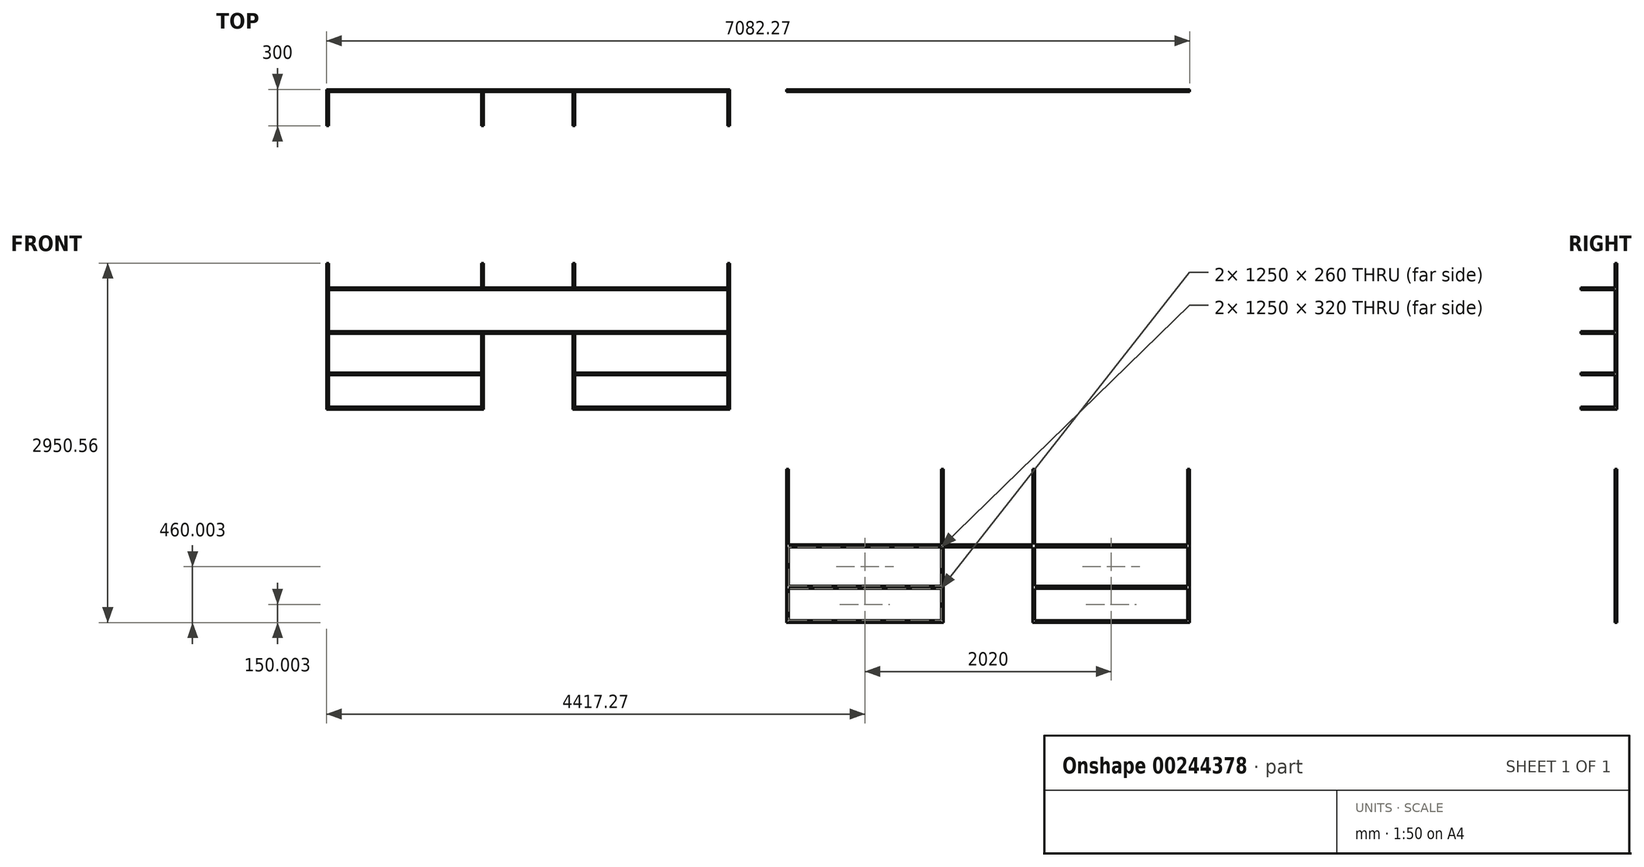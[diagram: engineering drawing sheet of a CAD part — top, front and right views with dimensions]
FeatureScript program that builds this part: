
annotation { "Feature Type Name" : "Feature", "Feature Type Description" : "" }
export const myFeature = defineFeature(function(context is Context, id is Id, definition is map)
    precondition{}
    {
        {
            var Q0;
            Q0=qCreatedBy(makeId("Front.planeOp"),FACE);
            var sketch = newSketch(context, id + "F0", { "sketchPlane" : qUnion([Q0])});
            skLineSegment(sketch, "E0.bottom", {"start": v(0, 0) * mm, "end": v(1290, 0) * mm});
            skLineSegment(sketch, "E0.top", {"start": v(0, 1000) * mm, "end": v(1290, 1000) * mm});
            skLineSegment(sketch, "E0.left", {"start": v(0, 0) * mm, "end": v(0, 1000) * mm});
            skLineSegment(sketch, "E0.right", {"start": v(1290, 0) * mm, "end": v(1290, 1000) * mm});
            skLineSegment(sketch, "E1.bottom", {"start": v(1290, 1000) * mm, "end": v(2020, 1000) * mm});
            skLineSegment(sketch, "E1.top", {"start": v(1290, 620) * mm, "end": v(2020, 620) * mm});
            skLineSegment(sketch, "E1.left", {"start": v(1290, 1000) * mm, "end": v(1290, 620) * mm});
            skLineSegment(sketch, "E1.right", {"start": v(2020, 1000) * mm, "end": v(2020, 620) * mm});
            skLineSegment(sketch, "E2.bottom", {"start": v(2020, 1000) * mm, "end": v(3310, 1000) * mm});
            skLineSegment(sketch, "E2.top", {"start": v(2020, 0) * mm, "end": v(3310, 0) * mm});
            skLineSegment(sketch, "E2.left", {"start": v(2020, 1000) * mm, "end": v(2020, 0) * mm});
            skLineSegment(sketch, "E2.right", {"start": v(3310, 1000) * mm, "end": v(3310, 0) * mm});
            skLineSegment(sketch, "E3", {"start": v(0, 300) * mm, "end": v(1290, 300) * mm});
            skLineSegment(sketch, "E4", {"start": v(0, 620) * mm, "end": v(1290, 620) * mm});
            skLineSegment(sketch, "E5", {"start": v(2020, 620) * mm, "end": v(3310, 620) * mm});
            skLineSegment(sketch, "E6", {"start": v(2020, 300) * mm, "end": v(3310, 300) * mm});
            skLineSegment(sketch, "E7", {"start": v(20, 1000) * mm, "end": v(20, 0) * mm});
            skLineSegment(sketch, "E8", {"start": v(1270, 1000) * mm, "end": v(1270, 0) * mm});
            skLineSegment(sketch, "E9", {"start": v(0, 980) * mm, "end": v(3310, 980) * mm});
            skLineSegment(sketch, "E10", {"start": v(0, 640) * mm, "end": v(3310, 640) * mm});
            skPoint(sketch, "E11.endSnap0", {"position": v(3310, 500) * mm});
            skLineSegment(sketch, "E12", {"start": v(0, 280) * mm, "end": v(1290, 280) * mm});
            skLineSegment(sketch, "E13", {"start": v(0, 20) * mm, "end": v(1290, 20) * mm});
            skLineSegment(sketch, "E14.trimOffspring", {"start": v(2020, 280) * mm, "end": v(3310, 280) * mm});
            skLineSegment(sketch, "E15.trimOffspring", {"start": v(2020, 20) * mm, "end": v(3310, 20) * mm});
            skLineSegment(sketch, "E16", {"start": v(2040, 980) * mm, "end": v(2040, 0) * mm});
            skLineSegment(sketch, "E17", {"start": v(3290, 1000) * mm, "end": v(3290, 0) * mm});
            skLineSegment(sketch, "E18.bottom", {"start": v(3772.27, -1750.56) * mm, "end": v(5062.27, -1750.56) * mm});
            skLineSegment(sketch, "E18.left", {"start": v(3772.27, -1750.56) * mm, "end": v(3772.27, -490.56) * mm});
            skLineSegment(sketch, "E18.right", {"start": v(5062.27, -1750.56) * mm, "end": v(5062.27, -490.56) * mm});
            skLineSegment(sketch, "E19.top", {"start": v(5062.27, -1130.56) * mm, "end": v(5792.27, -1130.56) * mm});
            skLineSegment(sketch, "E19.left", {"start": v(5062.27, -490.56) * mm, "end": v(5062.27, -1130.56) * mm});
            skLineSegment(sketch, "E19.right", {"start": v(5792.27, -490.56) * mm, "end": v(5792.27, -1130.56) * mm});
            skLineSegment(sketch, "E20.top", {"start": v(5792.27, -1750.56) * mm, "end": v(7082.27, -1750.56) * mm});
            skLineSegment(sketch, "E20.left", {"start": v(5792.27, -490.56) * mm, "end": v(5792.27, -1750.56) * mm});
            skLineSegment(sketch, "E20.right", {"start": v(7082.27, -490.56) * mm, "end": v(7082.27, -1750.56) * mm});
            skLineSegment(sketch, "E21", {"start": v(3772.27, -1450.56) * mm, "end": v(5062.27, -1450.56) * mm});
            skLineSegment(sketch, "E22", {"start": v(3772.27, -1130.56) * mm, "end": v(5062.27, -1130.56) * mm});
            skLineSegment(sketch, "E23", {"start": v(5792.27, -1130.56) * mm, "end": v(7082.27, -1130.56) * mm});
            skLineSegment(sketch, "E24", {"start": v(5792.27, -1450.56) * mm, "end": v(7082.27, -1450.56) * mm});
            skLineSegment(sketch, "E25", {"start": v(3792.27, -490.56) * mm, "end": v(3792.27, -1750.56) * mm});
            skLineSegment(sketch, "E26", {"start": v(5042.27, -490.56) * mm, "end": v(5042.27, -1750.56) * mm});
            skLineSegment(sketch, "E27", {"start": v(3772.27, -1110.56) * mm, "end": v(7082.27, -1110.56) * mm});
            skPoint(sketch, "E28.endSnap0", {"position": v(7082.27, -1120.56) * mm});
            skLineSegment(sketch, "E29", {"start": v(3772.27, -1470.56) * mm, "end": v(5062.27, -1470.56) * mm});
            skLineSegment(sketch, "E30", {"start": v(3772.27, -1730.56) * mm, "end": v(5062.27, -1730.56) * mm});
            skLineSegment(sketch, "E31.trimOffspring", {"start": v(5792.27, -1470.56) * mm, "end": v(7082.27, -1470.56) * mm});
            skLineSegment(sketch, "E32.trimOffspring", {"start": v(5792.27, -1730.56) * mm, "end": v(7082.27, -1730.56) * mm});
            skLineSegment(sketch, "E33", {"start": v(5812.27, -770.56) * mm, "end": v(5812.27, -1750.56) * mm});
            skLineSegment(sketch, "E34", {"start": v(7062.27, -490.56) * mm, "end": v(7062.27, -1750.56) * mm});
            skLineSegment(sketch, "E35", {"start": v(5812.27, -770.56) * mm, "end": v(5812.27, -490.56) * mm});
            skLineSegment(sketch, "E36.trimOffspring", {"start": v(5792.27, -770.56) * mm, "end": v(5812.27, -770.56) * mm});
            skLineSegment(sketch, "E37.trimOffspring", {"start": v(7062.27, -770.56) * mm, "end": v(7082.27, -770.56) * mm});
            skLineSegment(sketch, "E38.trimOffspring", {"start": v(7062.27, -490.56) * mm, "end": v(7082.27, -490.56) * mm});
            skLineSegment(sketch, "E39.trimOffspring", {"start": v(5042.27, -490.56) * mm, "end": v(5062.27, -490.56) * mm});
            skLineSegment(sketch, "E40.trimOffspring", {"start": v(5042.27, -770.56) * mm, "end": v(5062.27, -770.56) * mm});
            skLineSegment(sketch, "E41", {"start": v(3772.27, -490.56) * mm, "end": v(3792.27, -490.56) * mm});
            skLineSegment(sketch, "E42.bottom", {"start": v(0, 1000) * mm, "end": v(20, 1000) * mm});
            skLineSegment(sketch, "E42.top", {"start": v(0, 1200) * mm, "end": v(20, 1200) * mm});
            skLineSegment(sketch, "E42.left", {"start": v(0, 1000) * mm, "end": v(0, 1200) * mm});
            skLineSegment(sketch, "E42.right", {"start": v(20, 1000) * mm, "end": v(20, 1200) * mm});
            skLineSegment(sketch, "E43.bottom", {"start": v(1290, 1000) * mm, "end": v(1270, 1000) * mm});
            skLineSegment(sketch, "E43.top", {"start": v(1290, 1200) * mm, "end": v(1270, 1200) * mm});
            skLineSegment(sketch, "E43.left", {"start": v(1290, 1000) * mm, "end": v(1290, 1200) * mm});
            skLineSegment(sketch, "E43.right", {"start": v(1270, 1000) * mm, "end": v(1270, 1200) * mm});
            skLineSegment(sketch, "E44.bottom", {"start": v(2020, 1000) * mm, "end": v(2040, 1000) * mm});
            skLineSegment(sketch, "E44.top", {"start": v(2020, 1200) * mm, "end": v(2040, 1200) * mm});
            skLineSegment(sketch, "E44.left", {"start": v(2020, 1000) * mm, "end": v(2020, 1200) * mm});
            skLineSegment(sketch, "E44.right", {"start": v(2040, 1000) * mm, "end": v(2040, 1200) * mm});
            skLineSegment(sketch, "E45.bottom", {"start": v(3310, 1000) * mm, "end": v(3290, 1000) * mm});
            skLineSegment(sketch, "E45.top", {"start": v(3310, 1200) * mm, "end": v(3290, 1200) * mm});
            skLineSegment(sketch, "E45.left", {"start": v(3310, 1000) * mm, "end": v(3310, 1200) * mm});
            skLineSegment(sketch, "E45.right", {"start": v(3290, 1000) * mm, "end": v(3290, 1200) * mm});
            skLineSegment(sketch, "E46", {"start": v(5812.27, -490.56) * mm, "end": v(5792.27, -490.56) * mm});
            skSolve(sketch);
        }
        {
            var Q0;
            Q0 = qSketchRegion(id + "F0", true);
            var Q1;
            {var subQ0=sQuery(id+"F0.wireOp",EDGE,"E7");var subQ1=sQuery(id+"F0.wireOp",EDGE,"E4");var subQ2=makeQuery(id+"F0.imprint","INTERSECT",VERTEX,{"derivedFrom":[subQ1,subQ0]});Q1=makeQuery(id+"F0.imprint","IMPRINT",FACE,{"disambiguationData":[TD([[makeQuery(id+"F0.imprint","IMPRINT",EDGE,{"disambiguationData":[TD([[subQ2,-1.0]])],"derivedFrom":subQ1}),1.0]])]});}
            var Q2;
            {var subQ0=sQuery(id+"F0.wireOp",EDGE,"E7");var subQ1=sQuery(id+"F0.wireOp",EDGE,"E3");var subQ2=makeQuery(id+"F0.imprint","INTERSECT",VERTEX,{"derivedFrom":[subQ1,subQ0]});Q2=makeQuery(id+"F0.imprint","IMPRINT",FACE,{"disambiguationData":[TD([[makeQuery(id+"F0.imprint","IMPRINT",EDGE,{"disambiguationData":[TD([[subQ2,-1.0]])],"derivedFrom":subQ1}),-1.0]])]});}
            var Q3;
            {var subQ0=sQuery(id+"F0.wireOp",EDGE,"E9");var subQ1=sQuery(id+"F0.wireOp",EDGE,"E1.left");var subQ2=makeQuery(id+"F0.imprint","INTERSECT",VERTEX,{"derivedFrom":[subQ1,subQ0]});Q3=makeQuery(id+"F0.imprint","IMPRINT",FACE,{"disambiguationData":[TD([[makeQuery(id+"F0.imprint","IMPRINT",EDGE,{"disambiguationData":[TD([[subQ2,-1.0]])],"derivedFrom":subQ1}),-1.0]])]});}
            var Q4;
            {var subQ0=sQuery(id+"F0.wireOp",EDGE,"E9");var subQ1=sQuery(id+"F0.wireOp",EDGE,"E2.left");var subQ2=makeQuery(id+"F0.imprint","INTERSECT",VERTEX,{"derivedFrom":[subQ1,subQ0]});Q4=makeQuery(id+"F0.imprint","IMPRINT",FACE,{"disambiguationData":[TD([[makeQuery(id+"F0.imprint","IMPRINT",EDGE,{"disambiguationData":[TD([[subQ2,-1.0]])],"derivedFrom":subQ1}),1.0]])]});}
            var Q5;
            {var subQ0=sQuery(id+"F0.wireOp",EDGE,"E16");var subQ1=sQuery(id+"F0.wireOp",EDGE,"E5");var subQ2=makeQuery(id+"F0.imprint","INTERSECT",VERTEX,{"derivedFrom":[subQ1,subQ0]});Q5=makeQuery(id+"F0.imprint","IMPRINT",FACE,{"disambiguationData":[TD([[makeQuery(id+"F0.imprint","IMPRINT",EDGE,{"disambiguationData":[TD([[subQ2,-1.0]])],"derivedFrom":subQ1}),1.0]])]});}
            var Q6;
            {var subQ0=sQuery(id+"F0.wireOp",EDGE,"E16");var subQ1=sQuery(id+"F0.wireOp",EDGE,"E6");var subQ2=makeQuery(id+"F0.imprint","INTERSECT",VERTEX,{"derivedFrom":[subQ1,subQ0]});Q6=makeQuery(id+"F0.imprint","IMPRINT",FACE,{"disambiguationData":[TD([[makeQuery(id+"F0.imprint","IMPRINT",EDGE,{"disambiguationData":[TD([[subQ2,-1.0]])],"derivedFrom":subQ1}),-1.0]])]});}
            var Q7;
            {var subQ0=sQuery(id+"F0.wireOp",EDGE,"E25");var subQ1=sQuery(id+"F0.wireOp",EDGE,"E21");var subQ2=makeQuery(id+"F0.imprint","INTERSECT",VERTEX,{"derivedFrom":[subQ1,subQ0]});Q7=makeQuery(id+"F0.imprint","IMPRINT",FACE,{"disambiguationData":[TD([[makeQuery(id+"F0.imprint","IMPRINT",EDGE,{"disambiguationData":[TD([[subQ2,-1.0]])],"derivedFrom":subQ1}),-1.0]])]});}
            var Q8;
            {var subQ0=sQuery(id+"F0.wireOp",EDGE,"E33");var subQ1=sQuery(id+"F0.wireOp",EDGE,"E24");var subQ2=makeQuery(id+"F0.imprint","INTERSECT",VERTEX,{"derivedFrom":[subQ1,subQ0]});Q8=makeQuery(id+"F0.imprint","IMPRINT",FACE,{"disambiguationData":[TD([[makeQuery(id+"F0.imprint","IMPRINT",EDGE,{"disambiguationData":[TD([[subQ2,-1.0]])],"derivedFrom":subQ1}),-1.0]])]});}
            extrude(context, id + "F1", {"entities" : qUnion([Q0, Q1, Q2, Q3, Q4, Q5, Q6, Q7, Q8]), "depth" : 20 * mm});
        }
        {
            var Q0;
            Q0=makeQuery(id+"F1.opExtrude","CAP_FACE",FACE,{"disambiguationData":[OSD([sQuery(id+"F0.wireOp",EDGE,"E0.bottom"),sQuery(id+"F0.wireOp",EDGE,"E0.top"),sQuery(id+"F0.wireOp",EDGE,"E0.left"),sQuery(id+"F0.wireOp",EDGE,"E0.right"),sQuery(id+"F0.wireOp",EDGE,"E1.bottom"),sQuery(id+"F0.wireOp",EDGE,"E1.top"),sQuery(id+"F0.wireOp",EDGE,"E1.left"),sQuery(id+"F0.wireOp",EDGE,"E2.bottom"),sQuery(id+"F0.wireOp",EDGE,"E2.top"),sQuery(id+"F0.wireOp",EDGE,"E2.left"),sQuery(id+"F0.wireOp",EDGE,"E2.right"),sQuery(id+"F0.wireOp",EDGE,"E3"),sQuery(id+"F0.wireOp",EDGE,"E4"),sQuery(id+"F0.wireOp",EDGE,"E5"),sQuery(id+"F0.wireOp",EDGE,"E6"),sQuery(id+"F0.wireOp",EDGE,"E7"),sQuery(id+"F0.wireOp",EDGE,"E8"),sQuery(id+"F0.wireOp",EDGE,"E9"),sQuery(id+"F0.wireOp",EDGE,"E10"),sQuery(id+"F0.wireOp",EDGE,"E12"),sQuery(id+"F0.wireOp",EDGE,"E13"),sQuery(id+"F0.wireOp",EDGE,"E14.trimOffspring"),sQuery(id+"F0.wireOp",EDGE,"E15.trimOffspring"),sQuery(id+"F0.wireOp",EDGE,"E16"),sQuery(id+"F0.wireOp",EDGE,"E17"),sQuery(id+"F0.wireOp",EDGE,"E42.top"),sQuery(id+"F0.wireOp",EDGE,"E42.left"),sQuery(id+"F0.wireOp",EDGE,"E42.right"),sQuery(id+"F0.wireOp",EDGE,"E43.top"),sQuery(id+"F0.wireOp",EDGE,"E43.left"),sQuery(id+"F0.wireOp",EDGE,"E43.right"),sQuery(id+"F0.wireOp",EDGE,"E44.top"),sQuery(id+"F0.wireOp",EDGE,"E44.left"),sQuery(id+"F0.wireOp",EDGE,"E44.right"),sQuery(id+"F0.wireOp",EDGE,"E45.top"),sQuery(id+"F0.wireOp",EDGE,"E45.left"),sQuery(id+"F0.wireOp",EDGE,"E45.right")])],"isStart":false});
            var sketch = newSketch(context, id + "F2", { "sketchPlane" : qUnion([Q0])});
            skLineSegment(sketch, "E47.bottom", {"start": v(20, 980) * mm, "end": v(0, 980) * mm});
            skLineSegment(sketch, "E47.top", {"start": v(20, 1000) * mm, "end": v(0, 1000) * mm});
            skLineSegment(sketch, "E47.left", {"start": v(20, 980) * mm, "end": v(20, 1000) * mm});
            skLineSegment(sketch, "E47.right", {"start": v(0, 980) * mm, "end": v(0, 1000) * mm});
            skLineSegment(sketch, "E48.bottom", {"start": v(20, 620) * mm, "end": v(0, 620) * mm});
            skLineSegment(sketch, "E48.top", {"start": v(20, 640) * mm, "end": v(0, 640) * mm});
            skLineSegment(sketch, "E48.left", {"start": v(20, 620) * mm, "end": v(20, 640) * mm});
            skLineSegment(sketch, "E48.right", {"start": v(0, 620) * mm, "end": v(0, 640) * mm});
            skLineSegment(sketch, "E49.bottom", {"start": v(20, 280) * mm, "end": v(0, 280) * mm});
            skLineSegment(sketch, "E49.top", {"start": v(20, 300) * mm, "end": v(0, 300) * mm});
            skLineSegment(sketch, "E49.left", {"start": v(20, 280) * mm, "end": v(20, 300) * mm});
            skLineSegment(sketch, "E49.right", {"start": v(0, 280) * mm, "end": v(0, 300) * mm});
            skLineSegment(sketch, "E50.bottom", {"start": v(20, 20) * mm, "end": v(0, 20) * mm});
            skLineSegment(sketch, "E50.top", {"start": v(20, 0) * mm, "end": v(0, 0) * mm});
            skLineSegment(sketch, "E50.left", {"start": v(20, 20) * mm, "end": v(20, 0) * mm});
            skLineSegment(sketch, "E50.right", {"start": v(0, 20) * mm, "end": v(0, 0) * mm});
            skLineSegment(sketch, "E51", {"start": v(645, 980) * mm, "end": v(645, -184.5) * mm, "construction": true});
            skPoint(sketch, "E51.endSnap0", {"position": v(645, 0) * mm});
            skLineSegment(sketch, "E52.MirrorCS", {"start": v(1270, 300) * mm, "end": v(1290, 300) * mm});
            skLineSegment(sketch, "E53.MirrorCS", {"start": v(1270, 280) * mm, "end": v(1270, 300) * mm});
            skLineSegment(sketch, "E54.MirrorCS", {"start": v(1290, 980) * mm, "end": v(1290, 1000) * mm});
            skLineSegment(sketch, "E55.MirrorCS", {"start": v(1270, 1000) * mm, "end": v(1290, 1000) * mm});
            skLineSegment(sketch, "E56.MirrorCS", {"start": v(1290, 620) * mm, "end": v(1290, 640) * mm});
            skLineSegment(sketch, "E57.MirrorCS", {"start": v(1270, 280) * mm, "end": v(1290, 280) * mm});
            skLineSegment(sketch, "E58.MirrorCS", {"start": v(1270, 620) * mm, "end": v(1270, 640) * mm});
            skLineSegment(sketch, "E59.MirrorCS", {"start": v(1270, 20) * mm, "end": v(1290, 20) * mm});
            skLineSegment(sketch, "E60.MirrorCS", {"start": v(1290, 20) * mm, "end": v(1290, 0) * mm});
            skLineSegment(sketch, "E61.MirrorCS", {"start": v(1270, 980) * mm, "end": v(1290, 980) * mm});
            skLineSegment(sketch, "E62.MirrorCS", {"start": v(1270, 640) * mm, "end": v(1290, 640) * mm});
            skLineSegment(sketch, "E63.MirrorCS", {"start": v(1270, 20) * mm, "end": v(1270, 0) * mm});
            skLineSegment(sketch, "E64.MirrorCS", {"start": v(1270, 620) * mm, "end": v(1290, 620) * mm});
            skLineSegment(sketch, "E65.MirrorCS", {"start": v(1270, 0) * mm, "end": v(1290, 0) * mm});
            skLineSegment(sketch, "E66.MirrorCS", {"start": v(1270, 980) * mm, "end": v(1270, 1000) * mm});
            skLineSegment(sketch, "E67.MirrorCS", {"start": v(1290, 280) * mm, "end": v(1290, 300) * mm});
            skLineSegment(sketch, "E68", {"start": v(1655, 1000) * mm, "end": v(1655, 126.82) * mm, "construction": true});
            skPoint(sketch, "E68.endSnap0", {"position": v(1655, 980) * mm});
            skLineSegment(sketch, "E69.MirrorCS", {"start": v(2020, 620) * mm, "end": v(2020, 640) * mm});
            skLineSegment(sketch, "E70.MirrorCS", {"start": v(2020, 280) * mm, "end": v(2020, 300) * mm});
            skLineSegment(sketch, "E71.MirrorCS", {"start": v(2040, 20) * mm, "end": v(2020, 20) * mm});
            skLineSegment(sketch, "E72.MirrorCS", {"start": v(2040, 620) * mm, "end": v(2040, 640) * mm});
            skLineSegment(sketch, "E73.MirrorCS", {"start": v(3310, 20) * mm, "end": v(3310, 0) * mm});
            skLineSegment(sketch, "E74.MirrorCS", {"start": v(3290, 620) * mm, "end": v(3310, 620) * mm});
            skLineSegment(sketch, "E75.MirrorCS", {"start": v(2040, 300) * mm, "end": v(2020, 300) * mm});
            skLineSegment(sketch, "E76.MirrorCS", {"start": v(2040, 280) * mm, "end": v(2040, 300) * mm});
            skLineSegment(sketch, "E77.MirrorCS", {"start": v(3290, 280) * mm, "end": v(3290, 300) * mm});
            skLineSegment(sketch, "E78.MirrorCS", {"start": v(2020, 980) * mm, "end": v(2020, 1000) * mm});
            skLineSegment(sketch, "E79.MirrorCS", {"start": v(2040, 620) * mm, "end": v(2020, 620) * mm});
            skLineSegment(sketch, "E80.MirrorCS", {"start": v(3290, 300) * mm, "end": v(3310, 300) * mm});
            skLineSegment(sketch, "E81.MirrorCS", {"start": v(2040, 980) * mm, "end": v(2040, 1000) * mm});
            skLineSegment(sketch, "E82.MirrorCS", {"start": v(3290, 980) * mm, "end": v(3290, 1000) * mm});
            skLineSegment(sketch, "E83.MirrorCS", {"start": v(3290, 640) * mm, "end": v(3310, 640) * mm});
            skLineSegment(sketch, "E84.MirrorCS", {"start": v(3310, 620) * mm, "end": v(3310, 640) * mm});
            skLineSegment(sketch, "E85.MirrorCS", {"start": v(3290, 1000) * mm, "end": v(3310, 1000) * mm});
            skLineSegment(sketch, "E86.MirrorCS", {"start": v(3310, 280) * mm, "end": v(3310, 300) * mm});
            skLineSegment(sketch, "E87.MirrorCS", {"start": v(3290, 0) * mm, "end": v(3310, 0) * mm});
            skLineSegment(sketch, "E88.MirrorCS", {"start": v(2040, 980) * mm, "end": v(2020, 980) * mm});
            skLineSegment(sketch, "E89.MirrorCS", {"start": v(2040, 1000) * mm, "end": v(2020, 1000) * mm});
            skLineSegment(sketch, "E90.MirrorCS", {"start": v(3290, 280) * mm, "end": v(3310, 280) * mm});
            skLineSegment(sketch, "E91.MirrorCS", {"start": v(3290, 620) * mm, "end": v(3290, 640) * mm});
            skLineSegment(sketch, "E92.MirrorCS", {"start": v(2040, 0) * mm, "end": v(2020, 0) * mm});
            skLineSegment(sketch, "E93.MirrorCS", {"start": v(2040, 280) * mm, "end": v(2020, 280) * mm});
            skLineSegment(sketch, "E94.MirrorCS", {"start": v(3290, 20) * mm, "end": v(3310, 20) * mm});
            skLineSegment(sketch, "E95.MirrorCS", {"start": v(3290, 20) * mm, "end": v(3290, 0) * mm});
            skLineSegment(sketch, "E96.MirrorCS", {"start": v(2040, 20) * mm, "end": v(2040, 0) * mm});
            skLineSegment(sketch, "E97.MirrorCS", {"start": v(2020, 20) * mm, "end": v(2020, 0) * mm});
            skLineSegment(sketch, "E98.MirrorCS", {"start": v(3290, 980) * mm, "end": v(3310, 980) * mm});
            skLineSegment(sketch, "E99.MirrorCS", {"start": v(2040, 640) * mm, "end": v(2020, 640) * mm});
            skLineSegment(sketch, "E100.MirrorCS", {"start": v(3310, 980) * mm, "end": v(3310, 1000) * mm});
            skPoint(sketch, "E101.MirrorP", {"position": v(2665, 0) * mm});
            skSolve(sketch);
        }
        {
            var Q0;
            Q0 = qSketchRegion(id + "F2", true);
            extrude(context, id + "F3", {"entities" : qUnion([Q0]), "operationType" : NewBodyOperationType.ADD, "depth" : 280 * mm});
        }
    });
